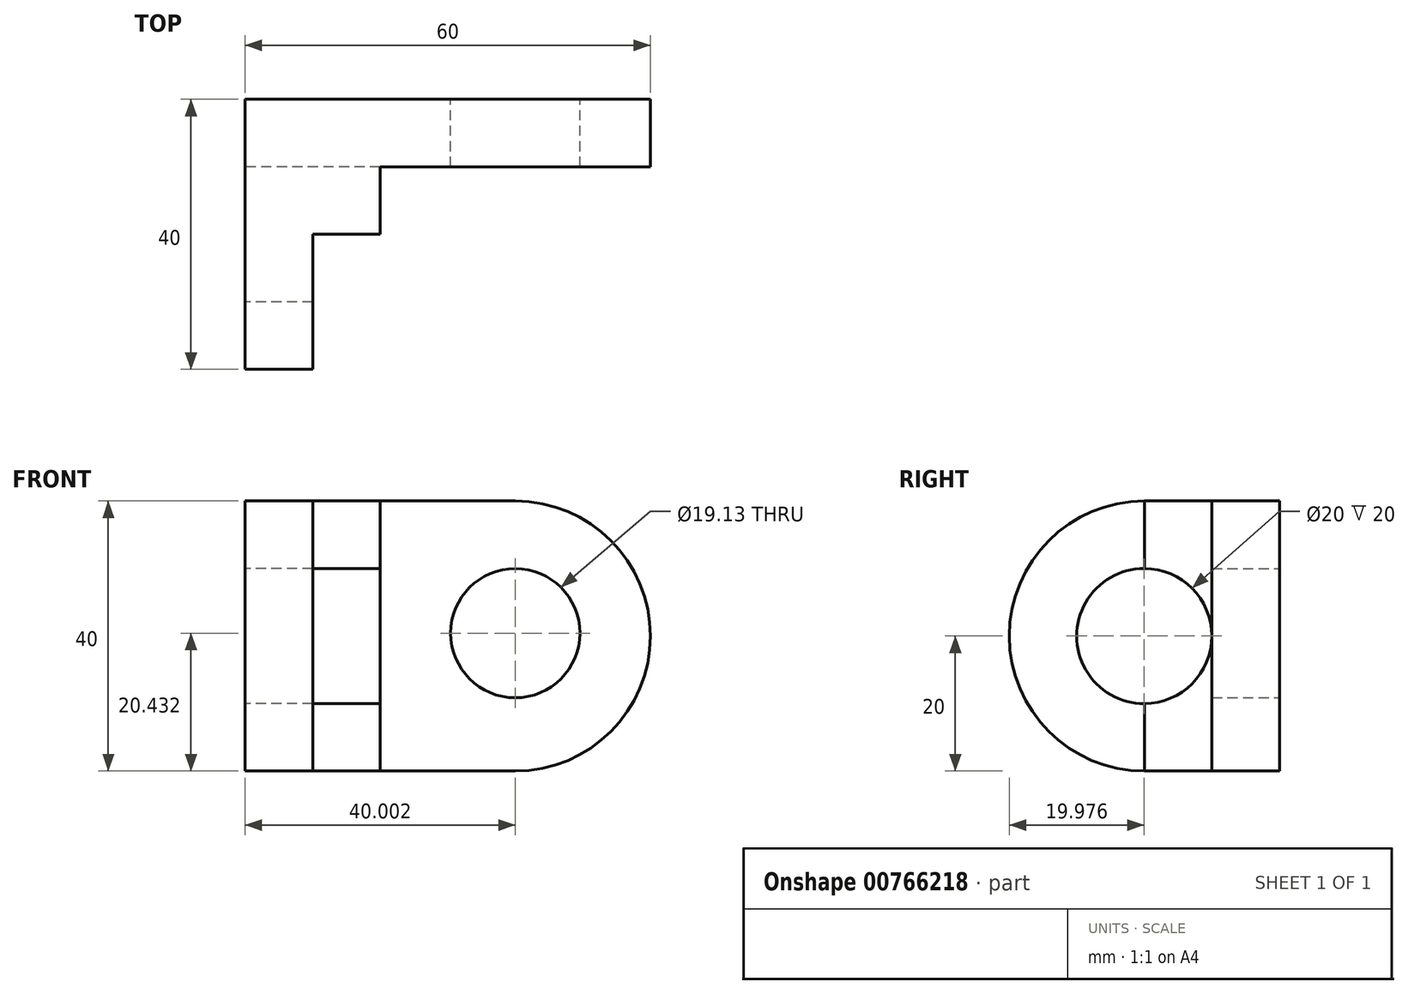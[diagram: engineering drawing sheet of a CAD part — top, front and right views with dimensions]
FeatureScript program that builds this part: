
annotation { "Feature Type Name" : "Feature", "Feature Type Description" : "" }
export const myFeature = defineFeature(function(context is Context, id is Id, definition is map)
    precondition{}
    {
        {
            var Q0;
            Q0=qCreatedBy(makeId("Front.planeOp"),FACE);
            var sketch = newSketch(context, id + "F0", { "sketchPlane" : qUnion([Q0])});
            skLineSegment(sketch, "E0.bottom", {"start": v(-20, 20) * mm, "end": v(20, 20) * mm});
            skLineSegment(sketch, "E0.top", {"start": v(-20, -20) * mm, "end": v(20, -20) * mm});
            skLineSegment(sketch, "E0.left", {"start": v(-20, 20) * mm, "end": v(-20, -20) * mm});
            skLineSegment(sketch, "E0.right", {"start": v(20, 20) * mm, "end": v(20, -20) * mm});
            skPoint(sketch, "E0.middle", {"position": v(0, 0) * mm});
            skArc(sketch, "E1", {"start": v(20, -20) * mm, "mid": v(40, 0) * mm, "end": v(20, 20) * mm});
            skLineSegment(sketch, "E2", {"start": v(20, 20) * mm, "end": v(20, 10) * mm});
            skLineSegment(sketch, "E3", {"start": v(20, -20) * mm, "end": v(20, -10) * mm});
            skCircle(sketch, "E4", {"center": v(20, 0.43) * mm, "radius": 9.57 * mm});
            skSolve(sketch);
        }
        {
            var Q0;
            Q0 = qSketchRegion(id + "F0", true);
            extrude(context, id + "F1", {"entities" : qUnion([Q0]), "depth" : 10 * mm, "offsetDistance" : 25 * mm});
        }
        {
            var Q0;
            Q0=makeQuery(id+"F1.opExtrude","CAP_FACE",FACE,{"disambiguationData":[OSD([sQuery(id+"F0.wireOp",EDGE,"E0.bottom"),sQuery(id+"F0.wireOp",EDGE,"E0.top"),sQuery(id+"F0.wireOp",EDGE,"E0.left"),sQuery(id+"F0.wireOp",EDGE,"E1"),sQuery(id+"F0.wireOp",EDGE,"E4")])],"isStart":false});
            var sketch = newSketch(context, id + "F2", { "sketchPlane" : qUnion([Q0])});
            skLineSegment(sketch, "E5", {"start": v(-20, 20) * mm, "end": v(0, 20) * mm});
            skLineSegment(sketch, "E6", {"start": v(0, 20) * mm, "end": v(0, -20) * mm});
            skLineSegment(sketch, "E7", {"start": v(0, -20) * mm, "end": v(-20, -20) * mm});
            skLineSegment(sketch, "E8", {"start": v(-20, -20) * mm, "end": v(-20, 20) * mm});
            skSolve(sketch);
        }
        {
            var Q0;
            Q0 = qSketchRegion(id + "F2", true);
            extrude(context, id + "F3", {"entities" : qUnion([Q0]), "operationType" : NewBodyOperationType.ADD, "depth" : 10 * mm, "offsetDistance" : 25 * mm});
        }
        {
            var Q0;
            Q0=makeQuery(id+"F3.opExtrude","CAP_FACE",FACE,{"disambiguationData":[OSD([sQuery(id+"F2.wireOp",EDGE,"E5"),sQuery(id+"F2.wireOp",EDGE,"E6"),sQuery(id+"F2.wireOp",EDGE,"E7"),sQuery(id+"F2.wireOp",EDGE,"E8")])],"isStart":false});
            var sketch = newSketch(context, id + "F4", { "sketchPlane" : qUnion([Q0])});
            skLineSegment(sketch, "E9", {"start": v(-20, -20) * mm, "end": v(-10, -20) * mm});
            skLineSegment(sketch, "E10", {"start": v(-10, -20) * mm, "end": v(-10, 20) * mm});
            skLineSegment(sketch, "E11", {"start": v(-10, 20) * mm, "end": v(-20, 20) * mm});
            skLineSegment(sketch, "E12", {"start": v(-20, 20) * mm, "end": v(-20, -20) * mm});
            skSolve(sketch);
        }
        {
            var Q0;
            Q0 = qSketchRegion(id + "F4", true);
            extrude(context, id + "F5", {"entities" : qUnion([Q0]), "operationType" : NewBodyOperationType.ADD, "depth" : 20 * mm, "offsetDistance" : 25 * mm});
        }
        {
            var Q0;
            Q0=makeQuery(id+"F5.opExtrude","SWEPT_FACE",FACE,{"disambiguationData":[OSD([sQuery(id+"F4.wireOp",EDGE,"E10")])]});
            var sketch = newSketch(context, id + "F6", { "sketchPlane" : qUnion([Q0])});
            skArc(sketch, "E13", {"start": v(-20, 20) * mm, "mid": v(-40, 0) * mm, "end": v(-20, -20) * mm});
            skSolve(sketch);
        }
        {
            var Q0;
            Q0=makeQuery(id+"F5.boolean.opBoolean","MERGE",FACE,{"derivedFrom":[makeQuery(id+"F3.boolean.opBoolean","MERGE",FACE,{"derivedFrom":[makeQuery(id+"F1.opExtrude","SWEPT_FACE",FACE,{"disambiguationData":[OSD([sQuery(id+"F0.wireOp",EDGE,"E0.left")])]}),makeQuery(id+"F3.opExtrude","SWEPT_FACE",FACE,{"disambiguationData":[OSD([sQuery(id+"F2.wireOp",EDGE,"E8")])]})]}),makeQuery(id+"F5.opExtrude","SWEPT_FACE",FACE,{"disambiguationData":[OSD([sQuery(id+"F4.wireOp",EDGE,"E12")])]})]});
            var sketch = newSketch(context, id + "F7", { "sketchPlane" : qUnion([Q0])});
            skCircle(sketch, "E14", {"center": v(20.02, 0) * mm, "radius": 10 * mm});
            skSolve(sketch);
        }
        {
            var Q0;
            Q0 = qSketchRegion(id + "F7", true);
            extrude(context, id + "F8", {"entities" : qUnion([Q0]), "operationType" : NewBodyOperationType.REMOVE, "oppositeDirection" : true, "depth" : 25 * mm, "offsetDistance" : 25 * mm});
        }
        {
            var Q0;
            {var subQ1=sQuery(id+"F4.wireOp",EDGE,"E10");var subQ2=makeQuery(id+"F5.opExtrude","SWEPT_EDGE",EDGE,{"disambiguationData":[OSD([sQuery(id+"F2.wireOp",EDGE,"E5"),subQ1,sQuery(id+"F4.wireOp",EDGE,"E11")])]});Q0=makeQuery(id+"F6.imprint","IMPRINT",FACE,{"disambiguationData":[TD([[makeQuery(id+"F6.imprint","IMPRINT",EDGE,{"derivedFrom":subQ2}),-1.0]])]});}
            extrude(context, id + "F9", {"entities" : qUnion([Q0]), "operationType" : NewBodyOperationType.REMOVE, "oppositeDirection" : true, "depth" : 25 * mm, "offsetDistance" : 25 * mm});
        }
        {
            var Q0;
            Q0=makeQuery(id+"F5.opExtrude","SWEPT_FACE",FACE,{"disambiguationData":[OSD([sQuery(id+"F4.wireOp",EDGE,"E10")])]});
            var sketch = newSketch(context, id + "F10", { "sketchPlane" : qUnion([Q0])});
            skArc(sketch, "E15", {"start": v(-20, 20) * mm, "mid": v(-40, 0) * mm, "end": v(-20, -20) * mm});
            skSolve(sketch);
        }
        {
            var Q0;
            {var subQ3=sQuery(id+"F4.wireOp",EDGE,"E10");var subQ5=makeQuery(id+"F5.opExtrude","CAP_EDGE",EDGE,{"disambiguationData":[OSD([subQ3])],"isStart":false});Q0=makeQuery(id+"F10.imprint","IMPRINT",FACE,{"disambiguationData":[TD([[makeQuery(id+"F10.imprint","IMPRINT",EDGE,{"derivedFrom":subQ5}),-1.0]])]});}
            extrude(context, id + "F11", {"entities" : qUnion([Q0]), "operationType" : NewBodyOperationType.REMOVE, "oppositeDirection" : true, "depth" : 25 * mm, "offsetDistance" : 25 * mm});
        }
    });
